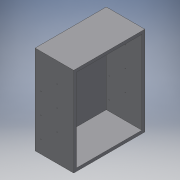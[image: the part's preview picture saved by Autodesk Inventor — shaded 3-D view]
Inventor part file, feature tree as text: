
AUTODESK INVENTOR PART (.ipt)
format: ipt  version: 2018 (Build 220112000, 112)  size: 155,136 bytes
history: native  units: in
note: dims shown in document units (in); Inventor stores cm internally (conversion verified against a paired STEP export)
features: extrude x3, sketch x2
ambient origin geometry x8: Origin, YZ Plane, XZ Plane, XY Plane, X Axis, Y Axis, Z Axis, Center Point
bodies: Solid1 (feature_tree)
feature tree (5):
  sketch  "Sketch1"  dims[d0=35.0in d1=24.0in]
  extrude  "Extrusion3"  Depth=24.0in
  extrude  "Extrusion4"  Depth=12.0in TaperAngle=0.0deg
  extrude  "Extrusion6"  Depth=1.0in TaperAngle=0.0deg
  sketch  "Sketch4"  dims[d2=1.0in d11=12.0in d12=0.0in d13=1.0in d14=0.0in d16=7.0in d17=7.0in d35=2.0in d36=1.1681in d37=2.0in d38=1.1681in d39=2.0in d40=1.1681in d44=36.0in d45=0.0in d46=4.0in d48=0.2031in d50=0.2031in d52=0.2031in d53=9.0in d54=0.9963in d55=9.0in d56=0.9963in d57=9.0in d58=0.9963in d59=0.2031in d60=0.2031in d61=0.2031in]
